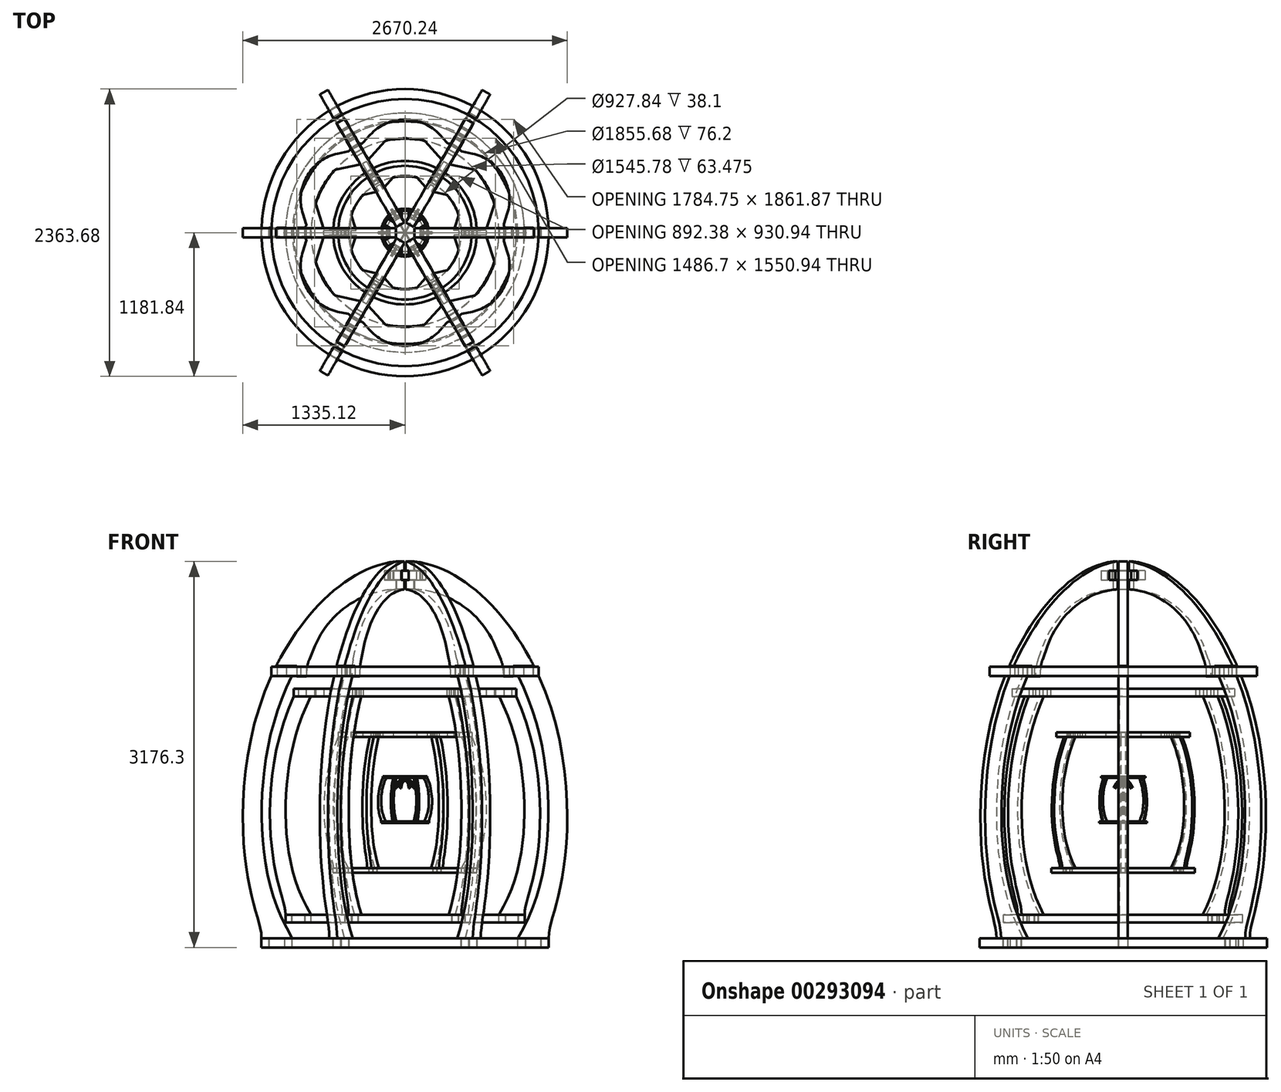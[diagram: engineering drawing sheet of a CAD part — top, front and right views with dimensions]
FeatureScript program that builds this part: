
annotation { "Feature Type Name" : "Feature", "Feature Type Description" : "" }
export const myFeature = defineFeature(function(context is Context, id is Id, definition is map)
    precondition{}
    {
        {
            var Q0;
            Q0=qCreatedBy(makeId("Front.planeOp"),FACE);
            var sketch = newSketch(context, id + "F0", { "sketchPlane" : qUnion([Q0])});
            skLineSegment(sketch, "E0", {"start": v(-1181.84, -1151.07) * mm, "end": v(-927.84, -1151.07) * mm});
            skFitSpline(sketch, "E1", {"points": [v(0, 1953.18) * mm, v(-1100.72, 1005.66) * mm, v(-1321.31, -446.19) * mm, v(-1216.83, -971.83) * mm, v(-1181.84, -1151.07) * mm], "startDerivative": vector(-4000.43, 5.06) * mm, "endDerivative": vector(0, -1489.55) * mm});
            skLineSegment(sketch, "E2", {"start": v(-1099.69, 1007.93) * mm, "end": v(-930.94, 1007.93) * mm});
            skLineSegment(sketch, "E3", {"start": v(-1181.84, -1151.07) * mm, "end": v(-1181.84, -1354.27) * mm});
            skLineSegment(sketch, "E4", {"start": v(-1181.84, -1354.27) * mm, "end": v(-877.04, -1354.27) * mm});
            skLineSegment(sketch, "E5", {"start": v(-877.04, -1354.27) * mm, "end": v(-877.04, -1252.67) * mm});
            skLineSegment(sketch, "E6", {"start": v(-877.04, -1252.67) * mm, "end": v(-927.84, -1252.67) * mm});
            skLineSegment(sketch, "E7", {"start": v(-927.84, -1252.67) * mm, "end": v(-927.84, -1151.07) * mm});
            skFitSpline(sketch, "E8.trimOffspring", {"points": [v(0, -1758.08) * mm, v(-927.84, -1151.07) * mm, v(-1179.31, -127.97) * mm, v(-917.89, 1033.92) * mm, v(0, 1800.5) * mm], "startDerivative": vector(-4973.2, 113.59) * mm, "endDerivative": vector(4756.7, 336.76) * mm});
            skLineSegment(sketch, "E9", {"start": v(-1023.33, 1160.33) * mm, "end": v(-848.12, 1160.33) * mm});
            skLineSegment(sketch, "E10", {"start": v(0, 1953.18) * mm, "end": v(0, 1800.5) * mm});
            skLineSegment(sketch, "E11.bottom", {"start": v(-1118.34, -1074.87) * mm, "end": v(-991.34, -1074.87) * mm});
            skLineSegment(sketch, "E11.top", {"start": v(-1118.34, -1227.27) * mm, "end": v(-991.34, -1227.27) * mm});
            skLineSegment(sketch, "E11.left", {"start": v(-1118.34, -1074.87) * mm, "end": v(-1118.34, -1227.27) * mm});
            skLineSegment(sketch, "E11.right", {"start": v(-991.34, -1074.87) * mm, "end": v(-991.34, -1227.27) * mm});
            skPoint(sketch, "E11.middle", {"position": v(-1054.84, -1151.07) * mm});
            skLineSegment(sketch, "E12.bottom", {"start": v(-1053.41, 1084.13) * mm, "end": v(-977.21, 1084.13) * mm});
            skLineSegment(sketch, "E12.top", {"start": v(-1053.41, 931.73) * mm, "end": v(-977.21, 931.73) * mm});
            skLineSegment(sketch, "E12.left", {"start": v(-1053.41, 1084.13) * mm, "end": v(-1053.41, 931.73) * mm});
            skLineSegment(sketch, "E12.right", {"start": v(-977.21, 1084.13) * mm, "end": v(-977.21, 931.73) * mm});
            skPoint(sketch, "E12.middle", {"position": v(-1015.31, 1007.93) * mm});
            skLineSegment(sketch, "E13", {"start": v(-891.46, 1084.13) * mm, "end": v(-1063.3, 1084.13) * mm});
            skLineSegment(sketch, "E14", {"start": v(-889.38, 1087.96) * mm, "end": v(-1061.37, 1087.96) * mm});
            skLineSegment(sketch, "E15", {"start": v(-76.2, 1949.03) * mm, "end": v(-76.2, 1791.14) * mm});
            skLineSegment(sketch, "E16", {"start": v(-76.2, 1791.14) * mm, "end": v(-76.2, 1796.63) * mm});
            skLineSegment(sketch, "E17", {"start": v(-76.2, 1796.63) * mm, "end": v(-127, 1796.63) * mm});
            skLineSegment(sketch, "E18", {"start": v(-127, 1796.63) * mm, "end": v(-127, 1872.83) * mm});
            skLineSegment(sketch, "E19", {"start": v(-127, 1872.83) * mm, "end": v(-76.2, 1872.83) * mm});
            skLineSegment(sketch, "E20", {"start": v(-889.38, 1087.96) * mm, "end": v(-810.8, 1087.96) * mm});
            skLineSegment(sketch, "E21", {"start": v(-810.8, 1087.96) * mm, "end": v(-680.59, 1399.26) * mm});
            skLineSegment(sketch, "E22", {"start": v(-810.8, 1087.96) * mm, "end": v(-810.8, 1004.5) * mm});
            skLineSegment(sketch, "E23", {"start": v(-889.38, 1087.96) * mm, "end": v(-889.38, 1004.5) * mm});
            skLineSegment(sketch, "E24", {"start": v(-889.38, 1004.5) * mm, "end": v(-810.8, 1004.5) * mm});
            skFitSpline(sketch, "E25", {"points": [v(-554.31, 1534.3) * mm, v(-76.2, 1720.43) * mm], "startDerivative": vector(464.08, 398.04) * mm, "endDerivative": vector(465.1, 29.66) * mm});
            skLineSegment(sketch, "E26", {"start": v(-76.2, 1720.43) * mm, "end": v(-76.2, 1791.14) * mm});
            skSolve(sketch);
        }
        {
            var Q0;
            {var subQ5=sQuery(id+"F0.wireOp",EDGE,"E12.bottom");Q0=makeQuery(id+"F0.imprint","IMPRINT",FACE,{"disambiguationData":[TD([[makeQuery(id+"F0.imprint","IMPRINT",EDGE,{"derivedFrom":subQ5}),-1.0]])]});}
            var Q1;
            {var subQ5=sQuery(id+"F0.wireOp",EDGE,"E11.top");Q1=makeQuery(id+"F0.imprint","IMPRINT",FACE,{"disambiguationData":[TD([[makeQuery(id+"F0.imprint","IMPRINT",EDGE,{"derivedFrom":subQ5}),1.0]])]});}
            var Q2;
            {var subQ0=sQuery(id+"F0.wireOp",EDGE,"E11.left");var subQ3=sQuery(id+"F0.wireOp",EDGE,"E0");var subQ4=makeQuery(id+"F0.imprint","INTERSECT",VERTEX,{"derivedFrom":[subQ3,subQ0]});Q2=makeQuery(id+"F0.imprint","IMPRINT",FACE,{"disambiguationData":[TD([[makeQuery(id+"F0.imprint","IMPRINT",EDGE,{"disambiguationData":[TD([[subQ4,-1.0]])],"derivedFrom":subQ3}),1.0]])]});}
            var Q3;
            {var subQ0=sQuery(id+"F0.wireOp",EDGE,"E2");var subQ1=sQuery(id+"F0.wireOp",EDGE,"E1");var subQ2=makeQuery(id+"F0.imprint","INTERSECT",VERTEX,{"derivedFrom":[subQ1,subQ0]});Q3=makeQuery(id+"F0.imprint","IMPRINT",FACE,{"disambiguationData":[TD([[makeQuery(id+"F0.imprint","IMPRINT",EDGE,{"disambiguationData":[TD([[subQ2,-1.0]])],"derivedFrom":subQ0}),-1.0]])]});}
            var Q4;
            {var subQ0=sQuery(id+"F0.wireOp",EDGE,"E8.trimOffspring");var subQ1=sQuery(id+"F0.wireOp",EDGE,"E2");var subQ2=makeQuery(id+"F0.imprint","INTERSECT",VERTEX,{"derivedFrom":[subQ1,subQ0]});Q4=makeQuery(id+"F0.imprint","IMPRINT",FACE,{"disambiguationData":[TD([[makeQuery(id+"F0.imprint","IMPRINT",EDGE,{"disambiguationData":[TD([[subQ2,1.0]])],"derivedFrom":subQ1}),-1.0]])]});}
            var Q5;
            {var subQ0=sQuery(id+"F0.wireOp",EDGE,"E12.left");var subQ5=sQuery(id+"F0.wireOp",EDGE,"E2");var subQ6=makeQuery(id+"F0.imprint","INTERSECT",VERTEX,{"derivedFrom":[subQ5,subQ0]});Q5=makeQuery(id+"F0.imprint","IMPRINT",FACE,{"disambiguationData":[TD([[makeQuery(id+"F0.imprint","IMPRINT",EDGE,{"disambiguationData":[TD([[subQ6,-1.0]])],"derivedFrom":subQ5}),-1.0]])]});}
            var Q6;
            {var subQ0=sQuery(id+"F0.wireOp",EDGE,"E12.left");var subQ1=sQuery(id+"F0.wireOp",EDGE,"E2");var subQ2=makeQuery(id+"F0.imprint","INTERSECT",VERTEX,{"derivedFrom":[subQ1,subQ0]});Q6=makeQuery(id+"F0.imprint","IMPRINT",FACE,{"disambiguationData":[TD([[makeQuery(id+"F0.imprint","IMPRINT",EDGE,{"disambiguationData":[TD([[subQ2,-1.0]])],"derivedFrom":subQ1}),1.0]])]});}
            extrude(context, id + "F1", {"entities" : qUnion([Q0, Q1, Q2, Q3, Q4, Q5, Q6]), "endBound" : BoundingType.SYMMETRIC, "depth" : 76.2 * mm});
        }
        {
            var Q0;
            Q0=makeQuery(id+"F1.opExtrude","SWEPT_BODY",BODY,{"disambiguationData":[OSD([sQuery(id+"F0.wireOp",EDGE,"E0"),sQuery(id+"F0.wireOp",EDGE,"E1"),sQuery(id+"F0.wireOp",EDGE,"E2"),sQuery(id+"F0.wireOp",EDGE,"E8.trimOffspring")])]});
            var Q1;
            Q1=sQuery(id+"F0.wireOp",EDGE,"E10");
            circularPattern(context, id + "F2", {"entities" : qUnion([Q0]), "axis" : qUnion([Q1]), "angle" : 360 * degree, "instanceCount" : 6, "equalSpace" : true});
        }
        {
            var Q0;
            Q0=qCreatedBy(makeId("Top.planeOp"),FACE);
            var Q1;
            Q1=sQuery(id+"F0.wireOp",VERTEX,"E8.trimOffspring.1.internal");
            cPlane(context, id + "F3", {"entities" : qUnion([Q0, Q1]), "cplaneType" : CPlaneType.PLANE_POINT, "offset" : 25.4 * mm, "width" : 152.4 * mm, "height" : 152.4 * mm});
        }
        {
            var Q0;
            Q0=qCreatedBy(id+"F3.planeOp",FACE);
            var sketch = newSketch(context, id + "F4", { "sketchPlane" : qUnion([Q0])});
            skCircle(sketch, "E27", {"center": v(0, 0) * mm, "radius": 1181.84 * mm});
            skCircle(sketch, "E28", {"center": v(0, 0) * mm, "radius": 927.84 * mm});
            skLineSegment(sketch, "E29.bottom", {"start": v(-1118.98, 38.73) * mm, "end": v(-990.7, 38.73) * mm});
            skLineSegment(sketch, "E29.top", {"start": v(-1118.98, -38.74) * mm, "end": v(-990.7, -38.74) * mm});
            skLineSegment(sketch, "E29.left", {"start": v(-1118.98, 38.73) * mm, "end": v(-1118.98, -38.74) * mm});
            skLineSegment(sketch, "E29.right", {"start": v(-990.7, 38.73) * mm, "end": v(-990.7, -38.74) * mm});
            skPoint(sketch, "E29.middle", {"position": v(-1054.84, 0) * mm});
            skLineSegment(sketch, "E30.1.0", {"start": v(-593.03, -949.7) * mm, "end": v(-528.9, -838.6) * mm});
            skLineSegment(sketch, "E30.1.1", {"start": v(-593.03, -949.7) * mm, "end": v(-525.94, -988.43) * mm});
            skLineSegment(sketch, "E30.1.2", {"start": v(-525.94, -988.43) * mm, "end": v(-461.8, -877.34) * mm});
            skLineSegment(sketch, "E30.1.3", {"start": v(-528.9, -838.6) * mm, "end": v(-461.8, -877.34) * mm});
            skLineSegment(sketch, "E30.2.0", {"start": v(525.94, -988.43) * mm, "end": v(461.8, -877.34) * mm});
            skLineSegment(sketch, "E30.2.1", {"start": v(525.94, -988.43) * mm, "end": v(593.03, -949.7) * mm});
            skLineSegment(sketch, "E30.2.2", {"start": v(593.03, -949.7) * mm, "end": v(528.9, -838.6) * mm});
            skLineSegment(sketch, "E30.2.3", {"start": v(461.8, -877.34) * mm, "end": v(528.9, -838.6) * mm});
            skLineSegment(sketch, "E30.3.0", {"start": v(1118.98, -38.74) * mm, "end": v(990.7, -38.74) * mm});
            skLineSegment(sketch, "E30.3.1", {"start": v(1118.98, -38.74) * mm, "end": v(1118.98, 38.73) * mm});
            skLineSegment(sketch, "E30.3.2", {"start": v(1118.98, 38.73) * mm, "end": v(990.7, 38.73) * mm});
            skLineSegment(sketch, "E30.3.3", {"start": v(990.7, -38.74) * mm, "end": v(990.7, 38.73) * mm});
            skLineSegment(sketch, "E30.4.0", {"start": v(593.03, 949.7) * mm, "end": v(528.9, 838.6) * mm});
            skLineSegment(sketch, "E30.4.1", {"start": v(593.03, 949.7) * mm, "end": v(525.94, 988.43) * mm});
            skLineSegment(sketch, "E30.4.2", {"start": v(525.94, 988.43) * mm, "end": v(461.8, 877.34) * mm});
            skLineSegment(sketch, "E30.4.3", {"start": v(528.9, 838.6) * mm, "end": v(461.8, 877.34) * mm});
            skLineSegment(sketch, "E30.5.0", {"start": v(-525.94, 988.43) * mm, "end": v(-461.8, 877.34) * mm});
            skLineSegment(sketch, "E30.5.1", {"start": v(-525.94, 988.43) * mm, "end": v(-593.03, 949.7) * mm});
            skLineSegment(sketch, "E30.5.2", {"start": v(-593.03, 949.7) * mm, "end": v(-528.9, 838.6) * mm});
            skLineSegment(sketch, "E30.5.3", {"start": v(-461.8, 877.34) * mm, "end": v(-528.9, 838.6) * mm});
            skSolve(sketch);
        }
        {
            var Q0;
            Q0=makeQuery(id+"F4.imprint","IMPRINT",FACE,{"disambiguationData":[TD([[makeQuery(id+"F4.imprint","IMPRINT",EDGE,{"derivedFrom":sQuery(id+"F4.wireOp",EDGE,"E27")}),1.0]])]});
            extrude(context, id + "F5", {"entities" : qUnion([Q0]), "oppositeDirection" : true, "depth" : 76.2 * mm});
        }
        {
            var Q0;
            Q0=qCreatedBy(makeId("Top.planeOp"),FACE);
            var Q1;
            Q1=sQuery(id+"F0.wireOp",VERTEX,"E2.end");
            cPlane(context, id + "F6", {"entities" : qUnion([Q0, Q1]), "cplaneType" : CPlaneType.PLANE_POINT, "offset" : 25.4 * mm, "width" : 152.4 * mm, "height" : 152.4 * mm});
        }
        {
            var Q0;
            Q0=qCreatedBy(id+"F6.planeOp",FACE);
            var sketch = newSketch(context, id + "F7", { "sketchPlane" : qUnion([Q0])});
            skCircle(sketch, "E31", {"center": v(0, 0) * mm, "radius": 1099.69 * mm});
            skCircle(sketch, "E32", {"center": v(0, 0) * mm, "radius": 930.94 * mm});
            skLineSegment(sketch, "E33.bottom", {"start": v(-1054.05, 38.74) * mm, "end": v(-976.58, 38.74) * mm});
            skLineSegment(sketch, "E33.top", {"start": v(-1054.05, -38.73) * mm, "end": v(-976.58, -38.73) * mm});
            skLineSegment(sketch, "E33.left", {"start": v(-1054.05, 38.74) * mm, "end": v(-1054.05, -38.73) * mm});
            skLineSegment(sketch, "E33.right", {"start": v(-976.58, 38.74) * mm, "end": v(-976.58, -38.73) * mm});
            skPoint(sketch, "E33.middle", {"position": v(-1015.31, 0) * mm});
            skLineSegment(sketch, "E34.1.0", {"start": v(-560.57, -893.46) * mm, "end": v(-521.83, -826.37) * mm});
            skLineSegment(sketch, "E34.1.1", {"start": v(-560.57, -893.46) * mm, "end": v(-493.48, -932.2) * mm});
            skLineSegment(sketch, "E34.1.2", {"start": v(-493.48, -932.2) * mm, "end": v(-454.74, -865.1) * mm});
            skLineSegment(sketch, "E34.1.3", {"start": v(-521.83, -826.37) * mm, "end": v(-454.74, -865.1) * mm});
            skLineSegment(sketch, "E34.2.0", {"start": v(493.48, -932.2) * mm, "end": v(454.74, -865.1) * mm});
            skLineSegment(sketch, "E34.2.1", {"start": v(493.48, -932.2) * mm, "end": v(560.57, -893.46) * mm});
            skLineSegment(sketch, "E34.2.2", {"start": v(560.57, -893.46) * mm, "end": v(521.83, -826.37) * mm});
            skLineSegment(sketch, "E34.2.3", {"start": v(454.74, -865.1) * mm, "end": v(521.83, -826.37) * mm});
            skLineSegment(sketch, "E34.3.0", {"start": v(1054.05, -38.74) * mm, "end": v(976.58, -38.74) * mm});
            skLineSegment(sketch, "E34.3.1", {"start": v(1054.05, -38.74) * mm, "end": v(1054.05, 38.73) * mm});
            skLineSegment(sketch, "E34.3.2", {"start": v(1054.05, 38.73) * mm, "end": v(976.58, 38.73) * mm});
            skLineSegment(sketch, "E34.3.3", {"start": v(976.58, -38.74) * mm, "end": v(976.58, 38.73) * mm});
            skLineSegment(sketch, "E34.4.0", {"start": v(560.57, 893.46) * mm, "end": v(521.83, 826.37) * mm});
            skLineSegment(sketch, "E34.4.1", {"start": v(560.57, 893.46) * mm, "end": v(493.48, 932.2) * mm});
            skLineSegment(sketch, "E34.4.2", {"start": v(493.48, 932.2) * mm, "end": v(454.74, 865.1) * mm});
            skLineSegment(sketch, "E34.4.3", {"start": v(521.83, 826.37) * mm, "end": v(454.74, 865.1) * mm});
            skLineSegment(sketch, "E34.5.0", {"start": v(-493.48, 932.2) * mm, "end": v(-454.74, 865.1) * mm});
            skLineSegment(sketch, "E34.5.1", {"start": v(-493.48, 932.2) * mm, "end": v(-560.57, 893.46) * mm});
            skLineSegment(sketch, "E34.5.2", {"start": v(-560.57, 893.46) * mm, "end": v(-521.83, 826.37) * mm});
            skLineSegment(sketch, "E34.5.3", {"start": v(-454.74, 865.1) * mm, "end": v(-521.83, 826.37) * mm});
            skLineSegment(sketch, "E35", {"start": v(-930.13, 38.73) * mm, "end": v(-803.13, 38.73) * mm});
            skLineSegment(sketch, "E36", {"start": v(-930.13, -38.74) * mm, "end": v(-803.13, -38.73) * mm});
            skLineSegment(sketch, "E37", {"start": v(-803.13, 38.74) * mm, "end": v(-803.13, -38.74) * mm, "construction": true});
            skLineSegment(sketch, "E38", {"start": v(-803.13, 0) * mm, "end": v(0, 0) * mm, "construction": true});
            skLineSegment(sketch, "E39", {"start": v(-803.13, 38.73) * mm, "end": v(-884.69, 289.77) * mm});
            skLineSegment(sketch, "E40", {"start": v(-803.13, -38.73) * mm, "end": v(-884.69, -289.77) * mm});
            skLineSegment(sketch, "E41.1.0", {"start": v(-435.11, -676.16) * mm, "end": v(-693.3, -621.28) * mm});
            skLineSegment(sketch, "E41.1.1", {"start": v(-498.61, -786.15) * mm, "end": v(-435.11, -676.16) * mm});
            skLineSegment(sketch, "E41.1.2", {"start": v(-431.52, -824.88) * mm, "end": v(-368.02, -714.9) * mm});
            skLineSegment(sketch, "E41.1.3", {"start": v(-368.02, -714.9) * mm, "end": v(-191.4, -911.05) * mm});
            skLineSegment(sketch, "E41.2.0", {"start": v(368.02, -714.9) * mm, "end": v(191.4, -911.05) * mm});
            skLineSegment(sketch, "E41.2.1", {"start": v(431.52, -824.88) * mm, "end": v(368.02, -714.9) * mm});
            skLineSegment(sketch, "E41.2.2", {"start": v(498.61, -786.15) * mm, "end": v(435.11, -676.16) * mm});
            skLineSegment(sketch, "E41.2.3", {"start": v(435.11, -676.16) * mm, "end": v(693.3, -621.28) * mm});
            skLineSegment(sketch, "E41.3.0", {"start": v(803.13, -38.74) * mm, "end": v(884.69, -289.77) * mm});
            skLineSegment(sketch, "E41.3.1", {"start": v(930.13, -38.74) * mm, "end": v(803.13, -38.74) * mm});
            skLineSegment(sketch, "E41.3.2", {"start": v(930.13, 38.73) * mm, "end": v(803.13, 38.73) * mm});
            skLineSegment(sketch, "E41.3.3", {"start": v(803.13, 38.73) * mm, "end": v(884.69, 289.77) * mm});
            skLineSegment(sketch, "E41.4.0", {"start": v(435.11, 676.16) * mm, "end": v(693.3, 621.28) * mm});
            skLineSegment(sketch, "E41.4.1", {"start": v(498.61, 786.15) * mm, "end": v(435.11, 676.16) * mm});
            skLineSegment(sketch, "E41.4.2", {"start": v(431.52, 824.88) * mm, "end": v(368.02, 714.9) * mm});
            skLineSegment(sketch, "E41.4.3", {"start": v(368.02, 714.9) * mm, "end": v(191.4, 911.05) * mm});
            skLineSegment(sketch, "E41.5.0", {"start": v(-368.02, 714.9) * mm, "end": v(-191.4, 911.05) * mm});
            skLineSegment(sketch, "E41.5.1", {"start": v(-431.52, 824.88) * mm, "end": v(-368.02, 714.9) * mm});
            skLineSegment(sketch, "E41.5.2", {"start": v(-498.61, 786.15) * mm, "end": v(-435.11, 676.16) * mm});
            skLineSegment(sketch, "E41.5.3", {"start": v(-435.11, 676.16) * mm, "end": v(-693.3, 621.28) * mm});
            skLineSegment(sketch, "E42", {"start": v(-892.38, 38.73) * mm, "end": v(-892.38, -38.74) * mm});
            skLineSegment(sketch, "E43.1.0", {"start": v(-479.73, -753.45) * mm, "end": v(-412.64, -792.19) * mm});
            skLineSegment(sketch, "E43.2.0", {"start": v(412.64, -792.19) * mm, "end": v(479.73, -753.45) * mm});
            skLineSegment(sketch, "E43.3.0", {"start": v(892.38, -38.74) * mm, "end": v(892.38, 38.73) * mm});
            skLineSegment(sketch, "E43.4.0", {"start": v(479.73, 753.45) * mm, "end": v(412.64, 792.19) * mm});
            skLineSegment(sketch, "E43.5.0", {"start": v(-412.64, 792.19) * mm, "end": v(-479.73, 753.45) * mm});
            skSolve(sketch);
        }
        {
            var Q0;
            Q0=makeQuery(id+"F7.imprint","IMPRINT",FACE,{"disambiguationData":[TD([[makeQuery(id+"F7.imprint","IMPRINT",EDGE,{"derivedFrom":sQuery(id+"F7.wireOp",EDGE,"E31")}),1.0]])]});
            var Q1;
            {var subQ0=sQuery(id+"F7.wireOp",EDGE,"E36");Q1=makeQuery(id+"F7.imprint","IMPRINT",FACE,{"disambiguationData":[TD([[makeQuery(id+"F7.imprint","IMPRINT",EDGE,{"derivedFrom":subQ0}),-1.0]])]});}
            var Q2;
            {var subQ0=sQuery(id+"F7.wireOp",EDGE,"E35");Q2=makeQuery(id+"F7.imprint","IMPRINT",FACE,{"disambiguationData":[TD([[makeQuery(id+"F7.imprint","IMPRINT",EDGE,{"derivedFrom":subQ0}),1.0]])]});}
            var Q3;
            {var subQ0=sQuery(id+"F7.wireOp",EDGE,"E41.5.2");Q3=makeQuery(id+"F7.imprint","IMPRINT",FACE,{"disambiguationData":[TD([[makeQuery(id+"F7.imprint","IMPRINT",EDGE,{"derivedFrom":subQ0}),-1.0]])]});}
            var Q4;
            {var subQ0=sQuery(id+"F7.wireOp",EDGE,"E41.5.0");Q4=makeQuery(id+"F7.imprint","IMPRINT",FACE,{"disambiguationData":[TD([[makeQuery(id+"F7.imprint","IMPRINT",EDGE,{"derivedFrom":subQ0}),1.0]])]});}
            var Q5;
            {var subQ0=sQuery(id+"F7.wireOp",EDGE,"E41.4.2");Q5=makeQuery(id+"F7.imprint","IMPRINT",FACE,{"disambiguationData":[TD([[makeQuery(id+"F7.imprint","IMPRINT",EDGE,{"derivedFrom":subQ0}),-1.0]])]});}
            var Q6;
            {var subQ0=sQuery(id+"F7.wireOp",EDGE,"E41.4.0");Q6=makeQuery(id+"F7.imprint","IMPRINT",FACE,{"disambiguationData":[TD([[makeQuery(id+"F7.imprint","IMPRINT",EDGE,{"derivedFrom":subQ0}),1.0]])]});}
            var Q7;
            {var subQ0=sQuery(id+"F7.wireOp",EDGE,"E41.3.2");Q7=makeQuery(id+"F7.imprint","IMPRINT",FACE,{"disambiguationData":[TD([[makeQuery(id+"F7.imprint","IMPRINT",EDGE,{"derivedFrom":subQ0}),-1.0]])]});}
            var Q8;
            {var subQ0=sQuery(id+"F7.wireOp",EDGE,"E41.3.0");Q8=makeQuery(id+"F7.imprint","IMPRINT",FACE,{"disambiguationData":[TD([[makeQuery(id+"F7.imprint","IMPRINT",EDGE,{"derivedFrom":subQ0}),1.0]])]});}
            var Q9;
            {var subQ0=sQuery(id+"F7.wireOp",EDGE,"E41.2.2");Q9=makeQuery(id+"F7.imprint","IMPRINT",FACE,{"disambiguationData":[TD([[makeQuery(id+"F7.imprint","IMPRINT",EDGE,{"derivedFrom":subQ0}),-1.0]])]});}
            var Q10;
            {var subQ0=sQuery(id+"F7.wireOp",EDGE,"E41.2.0");Q10=makeQuery(id+"F7.imprint","IMPRINT",FACE,{"disambiguationData":[TD([[makeQuery(id+"F7.imprint","IMPRINT",EDGE,{"derivedFrom":subQ0}),1.0]])]});}
            var Q11;
            {var subQ0=sQuery(id+"F7.wireOp",EDGE,"E41.1.2");Q11=makeQuery(id+"F7.imprint","IMPRINT",FACE,{"disambiguationData":[TD([[makeQuery(id+"F7.imprint","IMPRINT",EDGE,{"derivedFrom":subQ0}),-1.0]])]});}
            var Q12;
            {var subQ0=sQuery(id+"F7.wireOp",EDGE,"E41.1.0");Q12=makeQuery(id+"F7.imprint","IMPRINT",FACE,{"disambiguationData":[TD([[makeQuery(id+"F7.imprint","IMPRINT",EDGE,{"derivedFrom":subQ0}),1.0]])]});}
            var Q13;
            {var subQ3=sQuery(id+"F7.wireOp",EDGE,"E42");Q13=makeQuery(id+"F7.imprint","IMPRINT",FACE,{"disambiguationData":[TD([[makeQuery(id+"F7.imprint","IMPRINT",EDGE,{"derivedFrom":subQ3}),-1.0]])]});}
            var Q14;
            {var subQ5=sQuery(id+"F7.wireOp",EDGE,"E43.1.0");Q14=makeQuery(id+"F7.imprint","IMPRINT",FACE,{"disambiguationData":[TD([[makeQuery(id+"F7.imprint","IMPRINT",EDGE,{"derivedFrom":subQ5}),-1.0]])]});}
            var Q15;
            {var subQ5=sQuery(id+"F7.wireOp",EDGE,"E43.2.0");Q15=makeQuery(id+"F7.imprint","IMPRINT",FACE,{"disambiguationData":[TD([[makeQuery(id+"F7.imprint","IMPRINT",EDGE,{"derivedFrom":subQ5}),-1.0]])]});}
            var Q16;
            {var subQ5=sQuery(id+"F7.wireOp",EDGE,"E43.3.0");Q16=makeQuery(id+"F7.imprint","IMPRINT",FACE,{"disambiguationData":[TD([[makeQuery(id+"F7.imprint","IMPRINT",EDGE,{"derivedFrom":subQ5}),-1.0]])]});}
            var Q17;
            {var subQ5=sQuery(id+"F7.wireOp",EDGE,"E43.4.0");Q17=makeQuery(id+"F7.imprint","IMPRINT",FACE,{"disambiguationData":[TD([[makeQuery(id+"F7.imprint","IMPRINT",EDGE,{"derivedFrom":subQ5}),-1.0]])]});}
            var Q18;
            {var subQ5=sQuery(id+"F7.wireOp",EDGE,"E43.5.0");Q18=makeQuery(id+"F7.imprint","IMPRINT",FACE,{"disambiguationData":[TD([[makeQuery(id+"F7.imprint","IMPRINT",EDGE,{"derivedFrom":subQ5}),-1.0]])]});}
            extrude(context, id + "F8", {"entities" : qUnion([Q0, Q1, Q2, Q3, Q4, Q5, Q6, Q7, Q8, Q9, Q10, Q11, Q12, Q13, Q14, Q15, Q16, Q17, Q18]), "depth" : 76.2 * mm});
        }
        {
            var Q0;
            Q0=makeQuery(id+"F8.opExtrude","SWEPT_BODY",BODY,{"disambiguationData":[OSD([sQuery(id+"F7.wireOp",EDGE,"E31"),sQuery(id+"F7.wireOp",EDGE,"E32"),sQuery(id+"F7.wireOp",EDGE,"E33.bottom"),sQuery(id+"F7.wireOp",EDGE,"E33.top"),sQuery(id+"F7.wireOp",EDGE,"E33.left"),sQuery(id+"F7.wireOp",EDGE,"E33.right"),sQuery(id+"F7.wireOp",EDGE,"E34.1.0"),sQuery(id+"F7.wireOp",EDGE,"E34.1.1"),sQuery(id+"F7.wireOp",EDGE,"E34.1.2"),sQuery(id+"F7.wireOp",EDGE,"E34.1.3"),sQuery(id+"F7.wireOp",EDGE,"E34.2.0"),sQuery(id+"F7.wireOp",EDGE,"E34.2.1"),sQuery(id+"F7.wireOp",EDGE,"E34.2.2"),sQuery(id+"F7.wireOp",EDGE,"E34.2.3"),sQuery(id+"F7.wireOp",EDGE,"E34.3.0"),sQuery(id+"F7.wireOp",EDGE,"E34.3.1"),sQuery(id+"F7.wireOp",EDGE,"E34.3.2"),sQuery(id+"F7.wireOp",EDGE,"E34.3.3"),sQuery(id+"F7.wireOp",EDGE,"E34.4.0"),sQuery(id+"F7.wireOp",EDGE,"E34.4.1"),sQuery(id+"F7.wireOp",EDGE,"E34.4.2"),sQuery(id+"F7.wireOp",EDGE,"E34.4.3"),sQuery(id+"F7.wireOp",EDGE,"E34.5.0"),sQuery(id+"F7.wireOp",EDGE,"E34.5.1"),sQuery(id+"F7.wireOp",EDGE,"E34.5.2"),sQuery(id+"F7.wireOp",EDGE,"E34.5.3")])]});
            var Q1;
            Q1=makeQuery(id+"F1.opExtrude","SWEPT_BODY",BODY,{"disambiguationData":[OSD([sQuery(id+"F0.wireOp",EDGE,"E0"),sQuery(id+"F0.wireOp",EDGE,"E1"),sQuery(id+"F0.wireOp",EDGE,"E2"),sQuery(id+"F0.wireOp",EDGE,"E8.trimOffspring"),sQuery(id+"F0.wireOp",EDGE,"E11.top"),sQuery(id+"F0.wireOp",EDGE,"E11.left"),sQuery(id+"F0.wireOp",EDGE,"E11.right"),sQuery(id+"F0.wireOp",EDGE,"E12.bottom"),sQuery(id+"F0.wireOp",EDGE,"E12.left"),sQuery(id+"F0.wireOp",EDGE,"E12.right")])]});
            var Q2;
            Q2=makeQuery(id+"F2.opPattern","COPY",BODY,{"derivedFrom":makeQuery(id+"F1.opExtrude","SWEPT_BODY",BODY,{"disambiguationData":[OSD([sQuery(id+"F0.wireOp",EDGE,"E0"),sQuery(id+"F0.wireOp",EDGE,"E1"),sQuery(id+"F0.wireOp",EDGE,"E2"),sQuery(id+"F0.wireOp",EDGE,"E8.trimOffspring"),sQuery(id+"F0.wireOp",EDGE,"E11.top"),sQuery(id+"F0.wireOp",EDGE,"E11.left"),sQuery(id+"F0.wireOp",EDGE,"E11.right"),sQuery(id+"F0.wireOp",EDGE,"E12.bottom"),sQuery(id+"F0.wireOp",EDGE,"E12.left"),sQuery(id+"F0.wireOp",EDGE,"E12.right")])]}),"instanceName":"5"});
            var Q3;
            Q3=makeQuery(id+"F2.opPattern","COPY",BODY,{"derivedFrom":makeQuery(id+"F1.opExtrude","SWEPT_BODY",BODY,{"disambiguationData":[OSD([sQuery(id+"F0.wireOp",EDGE,"E0"),sQuery(id+"F0.wireOp",EDGE,"E1"),sQuery(id+"F0.wireOp",EDGE,"E2"),sQuery(id+"F0.wireOp",EDGE,"E8.trimOffspring"),sQuery(id+"F0.wireOp",EDGE,"E11.top"),sQuery(id+"F0.wireOp",EDGE,"E11.left"),sQuery(id+"F0.wireOp",EDGE,"E11.right"),sQuery(id+"F0.wireOp",EDGE,"E12.bottom"),sQuery(id+"F0.wireOp",EDGE,"E12.left"),sQuery(id+"F0.wireOp",EDGE,"E12.right")])]}),"instanceName":"1"});
            var Q4;
            Q4=makeQuery(id+"F2.opPattern","COPY",BODY,{"derivedFrom":makeQuery(id+"F1.opExtrude","SWEPT_BODY",BODY,{"disambiguationData":[OSD([sQuery(id+"F0.wireOp",EDGE,"E0"),sQuery(id+"F0.wireOp",EDGE,"E1"),sQuery(id+"F0.wireOp",EDGE,"E2"),sQuery(id+"F0.wireOp",EDGE,"E8.trimOffspring"),sQuery(id+"F0.wireOp",EDGE,"E11.top"),sQuery(id+"F0.wireOp",EDGE,"E11.left"),sQuery(id+"F0.wireOp",EDGE,"E11.right"),sQuery(id+"F0.wireOp",EDGE,"E12.bottom"),sQuery(id+"F0.wireOp",EDGE,"E12.left"),sQuery(id+"F0.wireOp",EDGE,"E12.right")])]}),"instanceName":"2"});
            var Q5;
            Q5=makeQuery(id+"F2.opPattern","COPY",BODY,{"derivedFrom":makeQuery(id+"F1.opExtrude","SWEPT_BODY",BODY,{"disambiguationData":[OSD([sQuery(id+"F0.wireOp",EDGE,"E0"),sQuery(id+"F0.wireOp",EDGE,"E1"),sQuery(id+"F0.wireOp",EDGE,"E2"),sQuery(id+"F0.wireOp",EDGE,"E8.trimOffspring"),sQuery(id+"F0.wireOp",EDGE,"E11.top"),sQuery(id+"F0.wireOp",EDGE,"E11.left"),sQuery(id+"F0.wireOp",EDGE,"E11.right"),sQuery(id+"F0.wireOp",EDGE,"E12.bottom"),sQuery(id+"F0.wireOp",EDGE,"E12.left"),sQuery(id+"F0.wireOp",EDGE,"E12.right")])]}),"instanceName":"3"});
            var Q6;
            Q6=makeQuery(id+"F2.opPattern","COPY",BODY,{"derivedFrom":makeQuery(id+"F1.opExtrude","SWEPT_BODY",BODY,{"disambiguationData":[OSD([sQuery(id+"F0.wireOp",EDGE,"E0"),sQuery(id+"F0.wireOp",EDGE,"E1"),sQuery(id+"F0.wireOp",EDGE,"E2"),sQuery(id+"F0.wireOp",EDGE,"E8.trimOffspring"),sQuery(id+"F0.wireOp",EDGE,"E11.top"),sQuery(id+"F0.wireOp",EDGE,"E11.left"),sQuery(id+"F0.wireOp",EDGE,"E11.right"),sQuery(id+"F0.wireOp",EDGE,"E12.bottom"),sQuery(id+"F0.wireOp",EDGE,"E12.left"),sQuery(id+"F0.wireOp",EDGE,"E12.right")])]}),"instanceName":"4"});
            var Q7;
            Q7=makeQuery(id+"F5.opExtrude","SWEPT_BODY",BODY,{"disambiguationData":[OSD([sQuery(id+"F4.wireOp",EDGE,"E27"),sQuery(id+"F4.wireOp",EDGE,"E28"),sQuery(id+"F4.wireOp",EDGE,"E29.bottom"),sQuery(id+"F4.wireOp",EDGE,"E29.top"),sQuery(id+"F4.wireOp",EDGE,"E29.left"),sQuery(id+"F4.wireOp",EDGE,"E29.right"),sQuery(id+"F4.wireOp",EDGE,"E30.1.0"),sQuery(id+"F4.wireOp",EDGE,"E30.1.1"),sQuery(id+"F4.wireOp",EDGE,"E30.1.2"),sQuery(id+"F4.wireOp",EDGE,"E30.1.3"),sQuery(id+"F4.wireOp",EDGE,"E30.2.0"),sQuery(id+"F4.wireOp",EDGE,"E30.2.1"),sQuery(id+"F4.wireOp",EDGE,"E30.2.2"),sQuery(id+"F4.wireOp",EDGE,"E30.2.3"),sQuery(id+"F4.wireOp",EDGE,"E30.3.0"),sQuery(id+"F4.wireOp",EDGE,"E30.3.1"),sQuery(id+"F4.wireOp",EDGE,"E30.3.2"),sQuery(id+"F4.wireOp",EDGE,"E30.3.3"),sQuery(id+"F4.wireOp",EDGE,"E30.4.0"),sQuery(id+"F4.wireOp",EDGE,"E30.4.1"),sQuery(id+"F4.wireOp",EDGE,"E30.4.2"),sQuery(id+"F4.wireOp",EDGE,"E30.4.3"),sQuery(id+"F4.wireOp",EDGE,"E30.5.0"),sQuery(id+"F4.wireOp",EDGE,"E30.5.1"),sQuery(id+"F4.wireOp",EDGE,"E30.5.2"),sQuery(id+"F4.wireOp",EDGE,"E30.5.3")])]});
            var Q8;
            Q8=qCreatedBy(makeId("Origin.pointOp"),VERTEX);
            transform(context, id + "F9", {"entities" : qUnion([Q0, Q1, Q2, Q3, Q4, Q5, Q6, Q7]), "transformType" : TransformType.SCALE_UNIFORMLY, "scale" : .1666, "scalePoint" : qUnion([Q8]), "makeCopy" : true});
        }
        {
            var Q0;
            Q0=makeQuery(id+"F8.opExtrude","SWEPT_BODY",BODY,{"disambiguationData":[OSD([sQuery(id+"F7.wireOp",EDGE,"E31"),sQuery(id+"F7.wireOp",EDGE,"E32"),sQuery(id+"F7.wireOp",EDGE,"E33.bottom"),sQuery(id+"F7.wireOp",EDGE,"E33.top"),sQuery(id+"F7.wireOp",EDGE,"E33.left"),sQuery(id+"F7.wireOp",EDGE,"E33.right"),sQuery(id+"F7.wireOp",EDGE,"E34.1.0"),sQuery(id+"F7.wireOp",EDGE,"E34.1.1"),sQuery(id+"F7.wireOp",EDGE,"E34.1.2"),sQuery(id+"F7.wireOp",EDGE,"E34.1.3"),sQuery(id+"F7.wireOp",EDGE,"E34.2.0"),sQuery(id+"F7.wireOp",EDGE,"E34.2.1"),sQuery(id+"F7.wireOp",EDGE,"E34.2.2"),sQuery(id+"F7.wireOp",EDGE,"E34.2.3"),sQuery(id+"F7.wireOp",EDGE,"E34.3.0"),sQuery(id+"F7.wireOp",EDGE,"E34.3.1"),sQuery(id+"F7.wireOp",EDGE,"E34.3.2"),sQuery(id+"F7.wireOp",EDGE,"E34.3.3"),sQuery(id+"F7.wireOp",EDGE,"E34.4.0"),sQuery(id+"F7.wireOp",EDGE,"E34.4.1"),sQuery(id+"F7.wireOp",EDGE,"E34.4.2"),sQuery(id+"F7.wireOp",EDGE,"E34.4.3"),sQuery(id+"F7.wireOp",EDGE,"E34.5.0"),sQuery(id+"F7.wireOp",EDGE,"E34.5.1"),sQuery(id+"F7.wireOp",EDGE,"E34.5.2"),sQuery(id+"F7.wireOp",EDGE,"E34.5.3")])]});
            var Q1;
            Q1=makeQuery(id+"F1.opExtrude","SWEPT_BODY",BODY,{"disambiguationData":[OSD([sQuery(id+"F0.wireOp",EDGE,"E0"),sQuery(id+"F0.wireOp",EDGE,"E1"),sQuery(id+"F0.wireOp",EDGE,"E2"),sQuery(id+"F0.wireOp",EDGE,"E8.trimOffspring"),sQuery(id+"F0.wireOp",EDGE,"E11.top"),sQuery(id+"F0.wireOp",EDGE,"E11.left"),sQuery(id+"F0.wireOp",EDGE,"E11.right"),sQuery(id+"F0.wireOp",EDGE,"E12.bottom"),sQuery(id+"F0.wireOp",EDGE,"E12.left"),sQuery(id+"F0.wireOp",EDGE,"E12.right")])]});
            var Q2;
            Q2=makeQuery(id+"F2.opPattern","COPY",BODY,{"derivedFrom":makeQuery(id+"F1.opExtrude","SWEPT_BODY",BODY,{"disambiguationData":[OSD([sQuery(id+"F0.wireOp",EDGE,"E0"),sQuery(id+"F0.wireOp",EDGE,"E1"),sQuery(id+"F0.wireOp",EDGE,"E2"),sQuery(id+"F0.wireOp",EDGE,"E8.trimOffspring"),sQuery(id+"F0.wireOp",EDGE,"E11.top"),sQuery(id+"F0.wireOp",EDGE,"E11.left"),sQuery(id+"F0.wireOp",EDGE,"E11.right"),sQuery(id+"F0.wireOp",EDGE,"E12.bottom"),sQuery(id+"F0.wireOp",EDGE,"E12.left"),sQuery(id+"F0.wireOp",EDGE,"E12.right")])]}),"instanceName":"1"});
            var Q3;
            Q3=makeQuery(id+"F2.opPattern","COPY",BODY,{"derivedFrom":makeQuery(id+"F1.opExtrude","SWEPT_BODY",BODY,{"disambiguationData":[OSD([sQuery(id+"F0.wireOp",EDGE,"E0"),sQuery(id+"F0.wireOp",EDGE,"E1"),sQuery(id+"F0.wireOp",EDGE,"E2"),sQuery(id+"F0.wireOp",EDGE,"E8.trimOffspring"),sQuery(id+"F0.wireOp",EDGE,"E11.top"),sQuery(id+"F0.wireOp",EDGE,"E11.left"),sQuery(id+"F0.wireOp",EDGE,"E11.right"),sQuery(id+"F0.wireOp",EDGE,"E12.bottom"),sQuery(id+"F0.wireOp",EDGE,"E12.left"),sQuery(id+"F0.wireOp",EDGE,"E12.right")])]}),"instanceName":"2"});
            var Q4;
            Q4=makeQuery(id+"F2.opPattern","COPY",BODY,{"derivedFrom":makeQuery(id+"F1.opExtrude","SWEPT_BODY",BODY,{"disambiguationData":[OSD([sQuery(id+"F0.wireOp",EDGE,"E0"),sQuery(id+"F0.wireOp",EDGE,"E1"),sQuery(id+"F0.wireOp",EDGE,"E2"),sQuery(id+"F0.wireOp",EDGE,"E8.trimOffspring"),sQuery(id+"F0.wireOp",EDGE,"E11.top"),sQuery(id+"F0.wireOp",EDGE,"E11.left"),sQuery(id+"F0.wireOp",EDGE,"E11.right"),sQuery(id+"F0.wireOp",EDGE,"E12.bottom"),sQuery(id+"F0.wireOp",EDGE,"E12.left"),sQuery(id+"F0.wireOp",EDGE,"E12.right")])]}),"instanceName":"3"});
            var Q5;
            Q5=makeQuery(id+"F2.opPattern","COPY",BODY,{"derivedFrom":makeQuery(id+"F1.opExtrude","SWEPT_BODY",BODY,{"disambiguationData":[OSD([sQuery(id+"F0.wireOp",EDGE,"E0"),sQuery(id+"F0.wireOp",EDGE,"E1"),sQuery(id+"F0.wireOp",EDGE,"E2"),sQuery(id+"F0.wireOp",EDGE,"E8.trimOffspring"),sQuery(id+"F0.wireOp",EDGE,"E11.top"),sQuery(id+"F0.wireOp",EDGE,"E11.left"),sQuery(id+"F0.wireOp",EDGE,"E11.right"),sQuery(id+"F0.wireOp",EDGE,"E12.bottom"),sQuery(id+"F0.wireOp",EDGE,"E12.left"),sQuery(id+"F0.wireOp",EDGE,"E12.right")])]}),"instanceName":"4"});
            var Q6;
            Q6=makeQuery(id+"F5.opExtrude","SWEPT_BODY",BODY,{"disambiguationData":[OSD([sQuery(id+"F4.wireOp",EDGE,"E27"),sQuery(id+"F4.wireOp",EDGE,"E28"),sQuery(id+"F4.wireOp",EDGE,"E29.bottom"),sQuery(id+"F4.wireOp",EDGE,"E29.top"),sQuery(id+"F4.wireOp",EDGE,"E29.left"),sQuery(id+"F4.wireOp",EDGE,"E29.right"),sQuery(id+"F4.wireOp",EDGE,"E30.1.0"),sQuery(id+"F4.wireOp",EDGE,"E30.1.1"),sQuery(id+"F4.wireOp",EDGE,"E30.1.2"),sQuery(id+"F4.wireOp",EDGE,"E30.1.3"),sQuery(id+"F4.wireOp",EDGE,"E30.2.0"),sQuery(id+"F4.wireOp",EDGE,"E30.2.1"),sQuery(id+"F4.wireOp",EDGE,"E30.2.2"),sQuery(id+"F4.wireOp",EDGE,"E30.2.3"),sQuery(id+"F4.wireOp",EDGE,"E30.3.0"),sQuery(id+"F4.wireOp",EDGE,"E30.3.1"),sQuery(id+"F4.wireOp",EDGE,"E30.3.2"),sQuery(id+"F4.wireOp",EDGE,"E30.3.3"),sQuery(id+"F4.wireOp",EDGE,"E30.4.0"),sQuery(id+"F4.wireOp",EDGE,"E30.4.1"),sQuery(id+"F4.wireOp",EDGE,"E30.4.2"),sQuery(id+"F4.wireOp",EDGE,"E30.4.3"),sQuery(id+"F4.wireOp",EDGE,"E30.5.0"),sQuery(id+"F4.wireOp",EDGE,"E30.5.1"),sQuery(id+"F4.wireOp",EDGE,"E30.5.2"),sQuery(id+"F4.wireOp",EDGE,"E30.5.3")])]});
            var Q7;
            Q7=makeQuery(id+"F2.opPattern","COPY",BODY,{"derivedFrom":makeQuery(id+"F1.opExtrude","SWEPT_BODY",BODY,{"disambiguationData":[OSD([sQuery(id+"F0.wireOp",EDGE,"E0"),sQuery(id+"F0.wireOp",EDGE,"E1"),sQuery(id+"F0.wireOp",EDGE,"E2"),sQuery(id+"F0.wireOp",EDGE,"E8.trimOffspring"),sQuery(id+"F0.wireOp",EDGE,"E11.top"),sQuery(id+"F0.wireOp",EDGE,"E11.left"),sQuery(id+"F0.wireOp",EDGE,"E11.right"),sQuery(id+"F0.wireOp",EDGE,"E12.bottom"),sQuery(id+"F0.wireOp",EDGE,"E12.left"),sQuery(id+"F0.wireOp",EDGE,"E12.right")])]}),"instanceName":"5"});
            var Q8;
            Q8=qCreatedBy(makeId("Origin.pointOp"),VERTEX);
            transform(context, id + "F10", {"entities" : qUnion([Q0, Q1, Q2, Q3, Q4, Q5, Q6, Q7]), "transformType" : TransformType.SCALE_UNIFORMLY, "scale" : .833, "scalePoint" : qUnion([Q8]), "makeCopy" : true});
        }
        {
            var Q0;
            Q0=makeQuery(id+"F8.opExtrude","SWEPT_BODY",BODY,{"disambiguationData":[OSD([sQuery(id+"F7.wireOp",EDGE,"E31"),sQuery(id+"F7.wireOp",EDGE,"E32"),sQuery(id+"F7.wireOp",EDGE,"E33.bottom"),sQuery(id+"F7.wireOp",EDGE,"E33.top"),sQuery(id+"F7.wireOp",EDGE,"E33.left"),sQuery(id+"F7.wireOp",EDGE,"E33.right"),sQuery(id+"F7.wireOp",EDGE,"E34.1.0"),sQuery(id+"F7.wireOp",EDGE,"E34.1.1"),sQuery(id+"F7.wireOp",EDGE,"E34.1.2"),sQuery(id+"F7.wireOp",EDGE,"E34.1.3"),sQuery(id+"F7.wireOp",EDGE,"E34.2.0"),sQuery(id+"F7.wireOp",EDGE,"E34.2.1"),sQuery(id+"F7.wireOp",EDGE,"E34.2.2"),sQuery(id+"F7.wireOp",EDGE,"E34.2.3"),sQuery(id+"F7.wireOp",EDGE,"E34.3.0"),sQuery(id+"F7.wireOp",EDGE,"E34.3.1"),sQuery(id+"F7.wireOp",EDGE,"E34.3.2"),sQuery(id+"F7.wireOp",EDGE,"E34.3.3"),sQuery(id+"F7.wireOp",EDGE,"E34.4.0"),sQuery(id+"F7.wireOp",EDGE,"E34.4.1"),sQuery(id+"F7.wireOp",EDGE,"E34.4.2"),sQuery(id+"F7.wireOp",EDGE,"E34.4.3"),sQuery(id+"F7.wireOp",EDGE,"E34.5.0"),sQuery(id+"F7.wireOp",EDGE,"E34.5.1"),sQuery(id+"F7.wireOp",EDGE,"E34.5.2"),sQuery(id+"F7.wireOp",EDGE,"E34.5.3")])]});
            var Q1;
            Q1=makeQuery(id+"F2.opPattern","COPY",BODY,{"derivedFrom":makeQuery(id+"F1.opExtrude","SWEPT_BODY",BODY,{"disambiguationData":[OSD([sQuery(id+"F0.wireOp",EDGE,"E0"),sQuery(id+"F0.wireOp",EDGE,"E1"),sQuery(id+"F0.wireOp",EDGE,"E2"),sQuery(id+"F0.wireOp",EDGE,"E8.trimOffspring"),sQuery(id+"F0.wireOp",EDGE,"E11.top"),sQuery(id+"F0.wireOp",EDGE,"E11.left"),sQuery(id+"F0.wireOp",EDGE,"E11.right"),sQuery(id+"F0.wireOp",EDGE,"E12.bottom"),sQuery(id+"F0.wireOp",EDGE,"E12.left"),sQuery(id+"F0.wireOp",EDGE,"E12.right")])]}),"instanceName":"5"});
            var Q2;
            Q2=makeQuery(id+"F1.opExtrude","SWEPT_BODY",BODY,{"disambiguationData":[OSD([sQuery(id+"F0.wireOp",EDGE,"E0"),sQuery(id+"F0.wireOp",EDGE,"E1"),sQuery(id+"F0.wireOp",EDGE,"E2"),sQuery(id+"F0.wireOp",EDGE,"E8.trimOffspring"),sQuery(id+"F0.wireOp",EDGE,"E11.top"),sQuery(id+"F0.wireOp",EDGE,"E11.left"),sQuery(id+"F0.wireOp",EDGE,"E11.right"),sQuery(id+"F0.wireOp",EDGE,"E12.bottom"),sQuery(id+"F0.wireOp",EDGE,"E12.left"),sQuery(id+"F0.wireOp",EDGE,"E12.right")])]});
            var Q3;
            Q3=makeQuery(id+"F2.opPattern","COPY",BODY,{"derivedFrom":makeQuery(id+"F1.opExtrude","SWEPT_BODY",BODY,{"disambiguationData":[OSD([sQuery(id+"F0.wireOp",EDGE,"E0"),sQuery(id+"F0.wireOp",EDGE,"E1"),sQuery(id+"F0.wireOp",EDGE,"E2"),sQuery(id+"F0.wireOp",EDGE,"E8.trimOffspring"),sQuery(id+"F0.wireOp",EDGE,"E11.top"),sQuery(id+"F0.wireOp",EDGE,"E11.left"),sQuery(id+"F0.wireOp",EDGE,"E11.right"),sQuery(id+"F0.wireOp",EDGE,"E12.bottom"),sQuery(id+"F0.wireOp",EDGE,"E12.left"),sQuery(id+"F0.wireOp",EDGE,"E12.right")])]}),"instanceName":"4"});
            var Q4;
            Q4=makeQuery(id+"F2.opPattern","COPY",BODY,{"derivedFrom":makeQuery(id+"F1.opExtrude","SWEPT_BODY",BODY,{"disambiguationData":[OSD([sQuery(id+"F0.wireOp",EDGE,"E0"),sQuery(id+"F0.wireOp",EDGE,"E1"),sQuery(id+"F0.wireOp",EDGE,"E2"),sQuery(id+"F0.wireOp",EDGE,"E8.trimOffspring"),sQuery(id+"F0.wireOp",EDGE,"E11.top"),sQuery(id+"F0.wireOp",EDGE,"E11.left"),sQuery(id+"F0.wireOp",EDGE,"E11.right"),sQuery(id+"F0.wireOp",EDGE,"E12.bottom"),sQuery(id+"F0.wireOp",EDGE,"E12.left"),sQuery(id+"F0.wireOp",EDGE,"E12.right")])]}),"instanceName":"3"});
            var Q5;
            Q5=makeQuery(id+"F2.opPattern","COPY",BODY,{"derivedFrom":makeQuery(id+"F1.opExtrude","SWEPT_BODY",BODY,{"disambiguationData":[OSD([sQuery(id+"F0.wireOp",EDGE,"E0"),sQuery(id+"F0.wireOp",EDGE,"E1"),sQuery(id+"F0.wireOp",EDGE,"E2"),sQuery(id+"F0.wireOp",EDGE,"E8.trimOffspring"),sQuery(id+"F0.wireOp",EDGE,"E11.top"),sQuery(id+"F0.wireOp",EDGE,"E11.left"),sQuery(id+"F0.wireOp",EDGE,"E11.right"),sQuery(id+"F0.wireOp",EDGE,"E12.bottom"),sQuery(id+"F0.wireOp",EDGE,"E12.left"),sQuery(id+"F0.wireOp",EDGE,"E12.right")])]}),"instanceName":"1"});
            var Q6;
            Q6=makeQuery(id+"F2.opPattern","COPY",BODY,{"derivedFrom":makeQuery(id+"F1.opExtrude","SWEPT_BODY",BODY,{"disambiguationData":[OSD([sQuery(id+"F0.wireOp",EDGE,"E0"),sQuery(id+"F0.wireOp",EDGE,"E1"),sQuery(id+"F0.wireOp",EDGE,"E2"),sQuery(id+"F0.wireOp",EDGE,"E8.trimOffspring"),sQuery(id+"F0.wireOp",EDGE,"E11.top"),sQuery(id+"F0.wireOp",EDGE,"E11.left"),sQuery(id+"F0.wireOp",EDGE,"E11.right"),sQuery(id+"F0.wireOp",EDGE,"E12.bottom"),sQuery(id+"F0.wireOp",EDGE,"E12.left"),sQuery(id+"F0.wireOp",EDGE,"E12.right")])]}),"instanceName":"2"});
            var Q7;
            Q7=makeQuery(id+"F5.opExtrude","SWEPT_BODY",BODY,{"disambiguationData":[OSD([sQuery(id+"F4.wireOp",EDGE,"E27"),sQuery(id+"F4.wireOp",EDGE,"E28"),sQuery(id+"F4.wireOp",EDGE,"E29.bottom"),sQuery(id+"F4.wireOp",EDGE,"E29.top"),sQuery(id+"F4.wireOp",EDGE,"E29.left"),sQuery(id+"F4.wireOp",EDGE,"E29.right"),sQuery(id+"F4.wireOp",EDGE,"E30.1.0"),sQuery(id+"F4.wireOp",EDGE,"E30.1.1"),sQuery(id+"F4.wireOp",EDGE,"E30.1.2"),sQuery(id+"F4.wireOp",EDGE,"E30.1.3"),sQuery(id+"F4.wireOp",EDGE,"E30.2.0"),sQuery(id+"F4.wireOp",EDGE,"E30.2.1"),sQuery(id+"F4.wireOp",EDGE,"E30.2.2"),sQuery(id+"F4.wireOp",EDGE,"E30.2.3"),sQuery(id+"F4.wireOp",EDGE,"E30.3.0"),sQuery(id+"F4.wireOp",EDGE,"E30.3.1"),sQuery(id+"F4.wireOp",EDGE,"E30.3.2"),sQuery(id+"F4.wireOp",EDGE,"E30.3.3"),sQuery(id+"F4.wireOp",EDGE,"E30.4.0"),sQuery(id+"F4.wireOp",EDGE,"E30.4.1"),sQuery(id+"F4.wireOp",EDGE,"E30.4.2"),sQuery(id+"F4.wireOp",EDGE,"E30.4.3"),sQuery(id+"F4.wireOp",EDGE,"E30.5.0"),sQuery(id+"F4.wireOp",EDGE,"E30.5.1"),sQuery(id+"F4.wireOp",EDGE,"E30.5.2"),sQuery(id+"F4.wireOp",EDGE,"E30.5.3")])]});
            var Q8;
            Q8=qCreatedBy(makeId("Origin.pointOp"),VERTEX);
            transform(context, id + "F11", {"entities" : qUnion([Q0, Q1, Q2, Q3, Q4, Q5, Q6, Q7]), "transformType" : TransformType.SCALE_UNIFORMLY, "scale" : .5, "scalePoint" : qUnion([Q8]), "makeCopy" : true});
        }
        {
            var Q0;
            {var subQ4=sQuery(id+"F0.wireOp",EDGE,"E9");Q0=makeQuery(id+"F0.imprint","IMPRINT",FACE,{"disambiguationData":[TD([[makeQuery(id+"F0.imprint","IMPRINT",EDGE,{"derivedFrom":subQ4}),-1.0]])]});}
            var Q1;
            {var subQ2=sQuery(id+"F0.wireOp",EDGE,"E9");Q1=makeQuery(id+"F0.imprint","IMPRINT",FACE,{"disambiguationData":[TD([[makeQuery(id+"F0.imprint","IMPRINT",EDGE,{"derivedFrom":subQ2}),1.0]])]});}
            var Q2;
            {var subQ2=sQuery(id+"F0.wireOp",EDGE,"E20");Q2=makeQuery(id+"F0.imprint","IMPRINT",FACE,{"disambiguationData":[TD([[makeQuery(id+"F0.imprint","IMPRINT",EDGE,{"derivedFrom":subQ2}),1.0]])]});}
            var Q3;
            Q3=makeQuery(id+"F0.imprint","IMPRINT",FACE,{"disambiguationData":[TD([[makeQuery(id+"F0.imprint","IMPRINT",EDGE,{"derivedFrom":sQuery(id+"F0.wireOp",EDGE,"E20")}),-1.0]])]});
            var Q4;
            {var subQ2=sQuery(id+"F0.wireOp",EDGE,"E25");Q4=makeQuery(id+"F0.imprint","IMPRINT",FACE,{"disambiguationData":[TD([[makeQuery(id+"F0.imprint","IMPRINT",EDGE,{"derivedFrom":subQ2}),1.0]])]});}
            extrude(context, id + "F12", {"entities" : qUnion([Q0, Q1, Q2, Q3, Q4]), "operationType" : NewBodyOperationType.ADD, "endBound" : BoundingType.SYMMETRIC, "depth" : 76.2 * mm});
        }
        {
            var Q0;
            Q0=makeQuery(id+"F12.opExtrude","SWEPT_EDGE",EDGE,{"disambiguationData":[OSD([sQuery(id+"F0.wireOp",EDGE,"E8.trimOffspring"),sQuery(id+"F0.wireOp",EDGE,"E21")])]});
            fillet(context, id + "F13", {"entities" : qUnion([Q0]), "radius" : 762 * mm, "tangentPropagation" : true, "allowEdgeOverflow" : false});
        }
        {
            var Q0;
            Q0=makeQuery(id+"F12.opExtrude","SWEPT_EDGE",EDGE,{"disambiguationData":[OSD([sQuery(id+"F0.wireOp",EDGE,"E20"),sQuery(id+"F0.wireOp",EDGE,"E21"),sQuery(id+"F0.wireOp",EDGE,"E22")])]});
            fillet(context, id + "F14", {"entities" : qUnion([Q0]), "radius" : 304.8 * mm, "tangentPropagation" : true, "allowEdgeOverflow" : false});
        }
        {
            var Q0;
            Q0=makeQuery(id+"F12.opExtrude","SWEPT_BODY",BODY,{"disambiguationData":[OSD([sQuery(id+"F0.wireOp",EDGE,"E1"),sQuery(id+"F0.wireOp",EDGE,"E8.trimOffspring"),sQuery(id+"F0.wireOp",EDGE,"E10"),sQuery(id+"F0.wireOp",EDGE,"E14")])]});
            var Q1;
            Q1=sQuery(id+"F0.wireOp",EDGE,"E10");
            circularPattern(context, id + "F15", {"entities" : qUnion([Q0]), "axis" : qUnion([Q1]), "angle" : 360 * degree, "instanceCount" : 6, "equalSpace" : true});
        }
        {
            var Q0;
            Q0=makeQuery(id+"F8.opExtrude","SWEPT_EDGE",EDGE,{"disambiguationData":[OSD([sQuery(id+"F7.wireOp",EDGE,"E32"),sQuery(id+"F7.wireOp",EDGE,"E40")])]});
            var Q1;
            Q1=makeQuery(id+"F8.opExtrude","SWEPT_EDGE",EDGE,{"disambiguationData":[OSD([sQuery(id+"F7.wireOp",EDGE,"E32"),sQuery(id+"F7.wireOp",EDGE,"E39")])]});
            var Q2;
            Q2=makeQuery(id+"F8.opExtrude","SWEPT_EDGE",EDGE,{"disambiguationData":[OSD([sQuery(id+"F7.wireOp",EDGE,"E32"),sQuery(id+"F7.wireOp",EDGE,"E41.5.3")])]});
            var Q3;
            Q3=makeQuery(id+"F8.opExtrude","SWEPT_EDGE",EDGE,{"disambiguationData":[OSD([sQuery(id+"F7.wireOp",EDGE,"E32"),sQuery(id+"F7.wireOp",EDGE,"E41.5.0")])]});
            var Q4;
            Q4=makeQuery(id+"F8.opExtrude","SWEPT_EDGE",EDGE,{"disambiguationData":[OSD([sQuery(id+"F7.wireOp",EDGE,"E32"),sQuery(id+"F7.wireOp",EDGE,"E41.4.3")])]});
            var Q5;
            Q5=makeQuery(id+"F8.opExtrude","SWEPT_EDGE",EDGE,{"disambiguationData":[OSD([sQuery(id+"F7.wireOp",EDGE,"E32"),sQuery(id+"F7.wireOp",EDGE,"E41.4.0")])]});
            var Q6;
            Q6=makeQuery(id+"F8.opExtrude","SWEPT_EDGE",EDGE,{"disambiguationData":[OSD([sQuery(id+"F7.wireOp",EDGE,"E32"),sQuery(id+"F7.wireOp",EDGE,"E41.3.3")])]});
            var Q7;
            Q7=makeQuery(id+"F8.opExtrude","SWEPT_EDGE",EDGE,{"disambiguationData":[OSD([sQuery(id+"F7.wireOp",EDGE,"E32"),sQuery(id+"F7.wireOp",EDGE,"E41.3.0")])]});
            var Q8;
            Q8=makeQuery(id+"F8.opExtrude","SWEPT_EDGE",EDGE,{"disambiguationData":[OSD([sQuery(id+"F7.wireOp",EDGE,"E32"),sQuery(id+"F7.wireOp",EDGE,"E41.2.3")])]});
            var Q9;
            Q9=makeQuery(id+"F8.opExtrude","SWEPT_EDGE",EDGE,{"disambiguationData":[OSD([sQuery(id+"F7.wireOp",EDGE,"E32"),sQuery(id+"F7.wireOp",EDGE,"E41.2.0")])]});
            var Q10;
            Q10=makeQuery(id+"F8.opExtrude","SWEPT_EDGE",EDGE,{"disambiguationData":[OSD([sQuery(id+"F7.wireOp",EDGE,"E32"),sQuery(id+"F7.wireOp",EDGE,"E41.1.3")])]});
            var Q11;
            Q11=makeQuery(id+"F8.opExtrude","SWEPT_EDGE",EDGE,{"disambiguationData":[OSD([sQuery(id+"F7.wireOp",EDGE,"E32"),sQuery(id+"F7.wireOp",EDGE,"E41.1.0")])]});
            fillet(context, id + "F16", {"entities" : qUnion([Q0, Q1, Q2, Q3, Q4, Q5, Q6, Q7, Q8, Q9, Q10, Q11]), "radius" : 381 * mm, "tangentPropagation" : true, "allowEdgeOverflow" : false});
        }
        {
            var Q0;
            Q0=makeQuery(id+"F8.opExtrude","SWEPT_EDGE",EDGE,{"disambiguationData":[OSD([sQuery(id+"F7.wireOp",EDGE,"E41.4.0"),sQuery(id+"F7.wireOp",EDGE,"E41.4.1")])]});
            var Q1;
            Q1=makeQuery(id+"F8.opExtrude","SWEPT_EDGE",EDGE,{"disambiguationData":[OSD([sQuery(id+"F7.wireOp",EDGE,"E41.4.2"),sQuery(id+"F7.wireOp",EDGE,"E41.4.3")])]});
            var Q2;
            Q2=makeQuery(id+"F8.opExtrude","SWEPT_EDGE",EDGE,{"disambiguationData":[OSD([sQuery(id+"F7.wireOp",EDGE,"E41.5.0"),sQuery(id+"F7.wireOp",EDGE,"E41.5.1")])]});
            var Q3;
            Q3=makeQuery(id+"F8.opExtrude","SWEPT_EDGE",EDGE,{"disambiguationData":[OSD([sQuery(id+"F7.wireOp",EDGE,"E41.5.2"),sQuery(id+"F7.wireOp",EDGE,"E41.5.3")])]});
            var Q4;
            Q4=makeQuery(id+"F8.opExtrude","SWEPT_EDGE",EDGE,{"disambiguationData":[OSD([sQuery(id+"F7.wireOp",EDGE,"E35"),sQuery(id+"F7.wireOp",EDGE,"E39")])]});
            var Q5;
            Q5=makeQuery(id+"F8.opExtrude","SWEPT_EDGE",EDGE,{"disambiguationData":[OSD([sQuery(id+"F7.wireOp",EDGE,"E36"),sQuery(id+"F7.wireOp",EDGE,"E40")])]});
            var Q6;
            Q6=makeQuery(id+"F8.opExtrude","SWEPT_EDGE",EDGE,{"disambiguationData":[OSD([sQuery(id+"F7.wireOp",EDGE,"E41.1.0"),sQuery(id+"F7.wireOp",EDGE,"E41.1.1")])]});
            var Q7;
            Q7=makeQuery(id+"F8.opExtrude","SWEPT_EDGE",EDGE,{"disambiguationData":[OSD([sQuery(id+"F7.wireOp",EDGE,"E41.1.2"),sQuery(id+"F7.wireOp",EDGE,"E41.1.3")])]});
            var Q8;
            Q8=makeQuery(id+"F8.opExtrude","SWEPT_EDGE",EDGE,{"disambiguationData":[OSD([sQuery(id+"F7.wireOp",EDGE,"E41.2.0"),sQuery(id+"F7.wireOp",EDGE,"E41.2.1")])]});
            var Q9;
            Q9=makeQuery(id+"F8.opExtrude","SWEPT_EDGE",EDGE,{"disambiguationData":[OSD([sQuery(id+"F7.wireOp",EDGE,"E41.2.2"),sQuery(id+"F7.wireOp",EDGE,"E41.2.3")])]});
            var Q10;
            Q10=makeQuery(id+"F8.opExtrude","SWEPT_EDGE",EDGE,{"disambiguationData":[OSD([sQuery(id+"F7.wireOp",EDGE,"E41.3.0"),sQuery(id+"F7.wireOp",EDGE,"E41.3.1")])]});
            var Q11;
            Q11=makeQuery(id+"F8.opExtrude","SWEPT_EDGE",EDGE,{"disambiguationData":[OSD([sQuery(id+"F7.wireOp",EDGE,"E41.3.2"),sQuery(id+"F7.wireOp",EDGE,"E41.3.3")])]});
            fillet(context, id + "F17", {"entities" : qUnion([Q0, Q1, Q2, Q3, Q4, Q5, Q6, Q7, Q8, Q9, Q10, Q11]), "radius" : 25.4 * mm, "tangentPropagation" : true, "allowEdgeOverflow" : false});
        }
        {
            var Q0;
            Q0=makeQuery(id+"F15.opPattern","COPY",FACE,{"derivedFrom":makeQuery(id+"F12.opExtrude","SWEPT_FACE",FACE,{"disambiguationData":[OSD([sQuery(id+"F0.wireOp",EDGE,"E17")])]}),"instanceName":"5"});
            var sketch = newSketch(context, id + "F18", { "sketchPlane" : qUnion([Q0])});
            skCircle(sketch, "E44", {"center": v(0, 0) * mm, "radius": 127 * mm});
            skLineSegment(sketch, "E45", {"start": v(-121.45, 37.13) * mm, "end": v(-170.95, 65.7) * mm});
            skLineSegment(sketch, "E46", {"start": v(-170.95, 65.7) * mm, "end": v(-142.37, 115.2) * mm});
            skLineSegment(sketch, "E47", {"start": v(-142.37, 115.2) * mm, "end": v(-92.88, 86.62) * mm});
            skLineSegment(sketch, "E48", {"start": v(-156.66, 90.45) * mm, "end": v(0, 0) * mm});
            skLineSegment(sketch, "E49", {"start": v(0, 0) * mm, "end": v(-54.91, 0) * mm, "construction": true});
            skLineSegment(sketch, "E50.1.0", {"start": v(-170.95, -65.7) * mm, "end": v(-121.45, -37.13) * mm});
            skLineSegment(sketch, "E50.1.1", {"start": v(-142.37, -115.2) * mm, "end": v(-170.95, -65.7) * mm});
            skLineSegment(sketch, "E50.1.2", {"start": v(-92.88, -86.62) * mm, "end": v(-142.37, -115.2) * mm});
            skLineSegment(sketch, "E50.2.0", {"start": v(-28.57, -180.9) * mm, "end": v(-28.57, -123.74) * mm});
            skLineSegment(sketch, "E50.2.1", {"start": v(28.58, -180.9) * mm, "end": v(-28.57, -180.9) * mm});
            skLineSegment(sketch, "E50.2.2", {"start": v(28.58, -123.74) * mm, "end": v(28.58, -180.9) * mm});
            skLineSegment(sketch, "E50.3.0", {"start": v(142.37, -115.2) * mm, "end": v(92.88, -86.62) * mm});
            skLineSegment(sketch, "E50.3.1", {"start": v(170.95, -65.7) * mm, "end": v(142.37, -115.2) * mm});
            skLineSegment(sketch, "E50.3.2", {"start": v(121.45, -37.13) * mm, "end": v(170.95, -65.7) * mm});
            skLineSegment(sketch, "E50.4.0", {"start": v(170.95, 65.7) * mm, "end": v(121.45, 37.13) * mm});
            skLineSegment(sketch, "E50.4.1", {"start": v(142.37, 115.2) * mm, "end": v(170.95, 65.7) * mm});
            skLineSegment(sketch, "E50.4.2", {"start": v(92.88, 86.62) * mm, "end": v(142.37, 115.2) * mm});
            skLineSegment(sketch, "E50.5.0", {"start": v(28.57, 180.9) * mm, "end": v(28.57, 123.74) * mm});
            skLineSegment(sketch, "E50.5.1", {"start": v(-28.58, 180.9) * mm, "end": v(28.57, 180.9) * mm});
            skLineSegment(sketch, "E50.5.2", {"start": v(-28.58, 123.74) * mm, "end": v(-28.58, 180.9) * mm});
            skSolve(sketch);
        }
        {
            var Q0;
            Q0=qSketchRegion(id+"F18",true);
            extrude(context, id + "F19", {"entities" : qUnion([Q0]), "depth" : 76.2 * mm});
        }
        {
            var Q0;
            Q0=makeQuery(id+"F15.opPattern","COPY",BODY,{"derivedFrom":makeQuery(id+"F12.opExtrude","SWEPT_BODY",BODY,{"disambiguationData":[OSD([sQuery(id+"F0.wireOp",EDGE,"E1"),sQuery(id+"F0.wireOp",EDGE,"E8.trimOffspring"),sQuery(id+"F0.wireOp",EDGE,"E14"),sQuery(id+"F0.wireOp",EDGE,"E15"),sQuery(id+"F0.wireOp",EDGE,"E16"),sQuery(id+"F0.wireOp",EDGE,"E17"),sQuery(id+"F0.wireOp",EDGE,"E18"),sQuery(id+"F0.wireOp",EDGE,"E19"),sQuery(id+"F0.wireOp",EDGE,"E21"),sQuery(id+"F0.wireOp",EDGE,"E22"),sQuery(id+"F0.wireOp",EDGE,"E23"),sQuery(id+"F0.wireOp",EDGE,"E24"),sQuery(id+"F0.wireOp",EDGE,"E25"),sQuery(id+"F0.wireOp",EDGE,"E26")])]}),"instanceName":"5"});
            var Q1;
            Q1=makeQuery(id+"F12.opExtrude","SWEPT_BODY",BODY,{"disambiguationData":[OSD([sQuery(id+"F0.wireOp",EDGE,"E1"),sQuery(id+"F0.wireOp",EDGE,"E8.trimOffspring"),sQuery(id+"F0.wireOp",EDGE,"E14"),sQuery(id+"F0.wireOp",EDGE,"E15"),sQuery(id+"F0.wireOp",EDGE,"E16"),sQuery(id+"F0.wireOp",EDGE,"E17"),sQuery(id+"F0.wireOp",EDGE,"E18"),sQuery(id+"F0.wireOp",EDGE,"E19"),sQuery(id+"F0.wireOp",EDGE,"E21"),sQuery(id+"F0.wireOp",EDGE,"E22"),sQuery(id+"F0.wireOp",EDGE,"E23"),sQuery(id+"F0.wireOp",EDGE,"E24"),sQuery(id+"F0.wireOp",EDGE,"E25"),sQuery(id+"F0.wireOp",EDGE,"E26")])]});
            var Q2;
            Q2=makeQuery(id+"F15.opPattern","COPY",BODY,{"derivedFrom":makeQuery(id+"F12.opExtrude","SWEPT_BODY",BODY,{"disambiguationData":[OSD([sQuery(id+"F0.wireOp",EDGE,"E1"),sQuery(id+"F0.wireOp",EDGE,"E8.trimOffspring"),sQuery(id+"F0.wireOp",EDGE,"E14"),sQuery(id+"F0.wireOp",EDGE,"E15"),sQuery(id+"F0.wireOp",EDGE,"E16"),sQuery(id+"F0.wireOp",EDGE,"E17"),sQuery(id+"F0.wireOp",EDGE,"E18"),sQuery(id+"F0.wireOp",EDGE,"E19"),sQuery(id+"F0.wireOp",EDGE,"E21"),sQuery(id+"F0.wireOp",EDGE,"E22"),sQuery(id+"F0.wireOp",EDGE,"E23"),sQuery(id+"F0.wireOp",EDGE,"E24"),sQuery(id+"F0.wireOp",EDGE,"E25"),sQuery(id+"F0.wireOp",EDGE,"E26")])]}),"instanceName":"3"});
            var Q3;
            Q3=makeQuery(id+"F15.opPattern","COPY",BODY,{"derivedFrom":makeQuery(id+"F12.opExtrude","SWEPT_BODY",BODY,{"disambiguationData":[OSD([sQuery(id+"F0.wireOp",EDGE,"E1"),sQuery(id+"F0.wireOp",EDGE,"E8.trimOffspring"),sQuery(id+"F0.wireOp",EDGE,"E14"),sQuery(id+"F0.wireOp",EDGE,"E15"),sQuery(id+"F0.wireOp",EDGE,"E16"),sQuery(id+"F0.wireOp",EDGE,"E17"),sQuery(id+"F0.wireOp",EDGE,"E18"),sQuery(id+"F0.wireOp",EDGE,"E19"),sQuery(id+"F0.wireOp",EDGE,"E21"),sQuery(id+"F0.wireOp",EDGE,"E22"),sQuery(id+"F0.wireOp",EDGE,"E23"),sQuery(id+"F0.wireOp",EDGE,"E24"),sQuery(id+"F0.wireOp",EDGE,"E25"),sQuery(id+"F0.wireOp",EDGE,"E26")])]}),"instanceName":"1"});
            var Q4;
            Q4=makeQuery(id+"F15.opPattern","COPY",BODY,{"derivedFrom":makeQuery(id+"F12.opExtrude","SWEPT_BODY",BODY,{"disambiguationData":[OSD([sQuery(id+"F0.wireOp",EDGE,"E1"),sQuery(id+"F0.wireOp",EDGE,"E8.trimOffspring"),sQuery(id+"F0.wireOp",EDGE,"E14"),sQuery(id+"F0.wireOp",EDGE,"E15"),sQuery(id+"F0.wireOp",EDGE,"E16"),sQuery(id+"F0.wireOp",EDGE,"E17"),sQuery(id+"F0.wireOp",EDGE,"E18"),sQuery(id+"F0.wireOp",EDGE,"E19"),sQuery(id+"F0.wireOp",EDGE,"E21"),sQuery(id+"F0.wireOp",EDGE,"E22"),sQuery(id+"F0.wireOp",EDGE,"E23"),sQuery(id+"F0.wireOp",EDGE,"E24"),sQuery(id+"F0.wireOp",EDGE,"E25"),sQuery(id+"F0.wireOp",EDGE,"E26")])]}),"instanceName":"2"});
            var Q5;
            Q5=makeQuery(id+"F15.opPattern","COPY",BODY,{"derivedFrom":makeQuery(id+"F12.opExtrude","SWEPT_BODY",BODY,{"disambiguationData":[OSD([sQuery(id+"F0.wireOp",EDGE,"E1"),sQuery(id+"F0.wireOp",EDGE,"E8.trimOffspring"),sQuery(id+"F0.wireOp",EDGE,"E14"),sQuery(id+"F0.wireOp",EDGE,"E15"),sQuery(id+"F0.wireOp",EDGE,"E16"),sQuery(id+"F0.wireOp",EDGE,"E17"),sQuery(id+"F0.wireOp",EDGE,"E18"),sQuery(id+"F0.wireOp",EDGE,"E19"),sQuery(id+"F0.wireOp",EDGE,"E21"),sQuery(id+"F0.wireOp",EDGE,"E22"),sQuery(id+"F0.wireOp",EDGE,"E23"),sQuery(id+"F0.wireOp",EDGE,"E24"),sQuery(id+"F0.wireOp",EDGE,"E25"),sQuery(id+"F0.wireOp",EDGE,"E26")])]}),"instanceName":"4"});
            var Q6;
            Q6=makeQuery(id+"F19.opExtrude","SWEPT_BODY",BODY,{"disambiguationData":[OSD([sQuery(id+"F18.wireOp",EDGE,"E44"),sQuery(id+"F18.wireOp",EDGE,"E45"),sQuery(id+"F18.wireOp",EDGE,"E46"),sQuery(id+"F18.wireOp",EDGE,"E47"),sQuery(id+"F18.wireOp",EDGE,"E50.1.0"),sQuery(id+"F18.wireOp",EDGE,"E50.1.1"),sQuery(id+"F18.wireOp",EDGE,"E50.1.2"),sQuery(id+"F18.wireOp",EDGE,"E50.2.0"),sQuery(id+"F18.wireOp",EDGE,"E50.2.1"),sQuery(id+"F18.wireOp",EDGE,"E50.2.2"),sQuery(id+"F18.wireOp",EDGE,"E50.3.0"),sQuery(id+"F18.wireOp",EDGE,"E50.3.1"),sQuery(id+"F18.wireOp",EDGE,"E50.3.2"),sQuery(id+"F18.wireOp",EDGE,"E50.4.0"),sQuery(id+"F18.wireOp",EDGE,"E50.4.1"),sQuery(id+"F18.wireOp",EDGE,"E50.4.2"),sQuery(id+"F18.wireOp",EDGE,"E50.5.0"),sQuery(id+"F18.wireOp",EDGE,"E50.5.1"),sQuery(id+"F18.wireOp",EDGE,"E50.5.2")])]});
            var Q7;
            Q7=qCreatedBy(makeId("Origin.pointOp"),VERTEX);
            transform(context, id + "F20", {"entities" : qUnion([Q0, Q1, Q2, Q3, Q4, Q5, Q6]), "transformType" : TransformType.SCALE_UNIFORMLY, "scale" : 1 / 12, "scalePoint" : qUnion([Q7]), "makeCopy" : true});
        }
        {
            var Q0;
            Q0=makeQuery(id+"F10.opPattern","COPY",EDGE,{"derivedFrom":makeQuery(id+"F8.opExtrude","SWEPT_EDGE",EDGE,{"disambiguationData":[OSD([sQuery(id+"F7.wireOp",EDGE,"E32"),sQuery(id+"F7.wireOp",EDGE,"E41.3.3")])]}),"instanceName":"1"});
            var Q1;
            Q1=makeQuery(id+"F10.opPattern","COPY",EDGE,{"derivedFrom":makeQuery(id+"F8.opExtrude","SWEPT_EDGE",EDGE,{"disambiguationData":[OSD([sQuery(id+"F7.wireOp",EDGE,"E32"),sQuery(id+"F7.wireOp",EDGE,"E41.4.0")])]}),"instanceName":"1"});
            var Q2;
            Q2=makeQuery(id+"F10.opPattern","COPY",EDGE,{"derivedFrom":makeQuery(id+"F8.opExtrude","SWEPT_EDGE",EDGE,{"disambiguationData":[OSD([sQuery(id+"F7.wireOp",EDGE,"E32"),sQuery(id+"F7.wireOp",EDGE,"E41.4.3")])]}),"instanceName":"1"});
            var Q3;
            Q3=makeQuery(id+"F10.opPattern","COPY",EDGE,{"derivedFrom":makeQuery(id+"F8.opExtrude","SWEPT_EDGE",EDGE,{"disambiguationData":[OSD([sQuery(id+"F7.wireOp",EDGE,"E32"),sQuery(id+"F7.wireOp",EDGE,"E41.5.0")])]}),"instanceName":"1"});
            var Q4;
            Q4=makeQuery(id+"F10.opPattern","COPY",EDGE,{"derivedFrom":makeQuery(id+"F8.opExtrude","SWEPT_EDGE",EDGE,{"disambiguationData":[OSD([sQuery(id+"F7.wireOp",EDGE,"E32"),sQuery(id+"F7.wireOp",EDGE,"E41.5.3")])]}),"instanceName":"1"});
            var Q5;
            Q5=makeQuery(id+"F10.opPattern","COPY",EDGE,{"derivedFrom":makeQuery(id+"F8.opExtrude","SWEPT_EDGE",EDGE,{"disambiguationData":[OSD([sQuery(id+"F7.wireOp",EDGE,"E32"),sQuery(id+"F7.wireOp",EDGE,"E39")])]}),"instanceName":"1"});
            var Q6;
            Q6=makeQuery(id+"F10.opPattern","COPY",EDGE,{"derivedFrom":makeQuery(id+"F8.opExtrude","SWEPT_EDGE",EDGE,{"disambiguationData":[OSD([sQuery(id+"F7.wireOp",EDGE,"E32"),sQuery(id+"F7.wireOp",EDGE,"E40")])]}),"instanceName":"1"});
            var Q7;
            Q7=makeQuery(id+"F10.opPattern","COPY",EDGE,{"derivedFrom":makeQuery(id+"F8.opExtrude","SWEPT_EDGE",EDGE,{"disambiguationData":[OSD([sQuery(id+"F7.wireOp",EDGE,"E32"),sQuery(id+"F7.wireOp",EDGE,"E41.1.0")])]}),"instanceName":"1"});
            var Q8;
            Q8=makeQuery(id+"F10.opPattern","COPY",EDGE,{"derivedFrom":makeQuery(id+"F8.opExtrude","SWEPT_EDGE",EDGE,{"disambiguationData":[OSD([sQuery(id+"F7.wireOp",EDGE,"E32"),sQuery(id+"F7.wireOp",EDGE,"E41.1.3")])]}),"instanceName":"1"});
            var Q9;
            Q9=makeQuery(id+"F10.opPattern","COPY",EDGE,{"derivedFrom":makeQuery(id+"F8.opExtrude","SWEPT_EDGE",EDGE,{"disambiguationData":[OSD([sQuery(id+"F7.wireOp",EDGE,"E32"),sQuery(id+"F7.wireOp",EDGE,"E41.2.0")])]}),"instanceName":"1"});
            var Q10;
            Q10=makeQuery(id+"F10.opPattern","COPY",EDGE,{"derivedFrom":makeQuery(id+"F8.opExtrude","SWEPT_EDGE",EDGE,{"disambiguationData":[OSD([sQuery(id+"F7.wireOp",EDGE,"E32"),sQuery(id+"F7.wireOp",EDGE,"E41.2.3")])]}),"instanceName":"1"});
            var Q11;
            Q11=makeQuery(id+"F10.opPattern","COPY",EDGE,{"derivedFrom":makeQuery(id+"F8.opExtrude","SWEPT_EDGE",EDGE,{"disambiguationData":[OSD([sQuery(id+"F7.wireOp",EDGE,"E32"),sQuery(id+"F7.wireOp",EDGE,"E41.3.0")])]}),"instanceName":"1"});
            fillet(context, id + "F21", {"entities" : qUnion([Q0, Q1, Q2, Q3, Q4, Q5, Q6, Q7, Q8, Q9, Q10, Q11]), "radius" : 31.75 * mm, "tangentPropagation" : true, "allowEdgeOverflow" : false});
        }
        {
            var Q0;
            Q0=makeQuery(id+"F10.opPattern","COPY",EDGE,{"derivedFrom":makeQuery(id+"F8.opExtrude","SWEPT_EDGE",EDGE,{"disambiguationData":[OSD([sQuery(id+"F7.wireOp",EDGE,"E41.3.2"),sQuery(id+"F7.wireOp",EDGE,"E41.3.3")])]}),"instanceName":"1"});
            var Q1;
            Q1=makeQuery(id+"F10.opPattern","COPY",EDGE,{"derivedFrom":makeQuery(id+"F8.opExtrude","SWEPT_EDGE",EDGE,{"disambiguationData":[OSD([sQuery(id+"F7.wireOp",EDGE,"E41.3.0"),sQuery(id+"F7.wireOp",EDGE,"E41.3.1")])]}),"instanceName":"1"});
            var Q2;
            Q2=makeQuery(id+"F10.opPattern","COPY",EDGE,{"derivedFrom":makeQuery(id+"F8.opExtrude","SWEPT_EDGE",EDGE,{"disambiguationData":[OSD([sQuery(id+"F7.wireOp",EDGE,"E41.2.2"),sQuery(id+"F7.wireOp",EDGE,"E41.2.3")])]}),"instanceName":"1"});
            var Q3;
            Q3=makeQuery(id+"F10.opPattern","COPY",EDGE,{"derivedFrom":makeQuery(id+"F8.opExtrude","SWEPT_EDGE",EDGE,{"disambiguationData":[OSD([sQuery(id+"F7.wireOp",EDGE,"E41.2.0"),sQuery(id+"F7.wireOp",EDGE,"E41.2.1")])]}),"instanceName":"1"});
            var Q4;
            Q4=makeQuery(id+"F10.opPattern","COPY",EDGE,{"derivedFrom":makeQuery(id+"F8.opExtrude","SWEPT_EDGE",EDGE,{"disambiguationData":[OSD([sQuery(id+"F7.wireOp",EDGE,"E41.1.2"),sQuery(id+"F7.wireOp",EDGE,"E41.1.3")])]}),"instanceName":"1"});
            var Q5;
            Q5=makeQuery(id+"F10.opPattern","COPY",EDGE,{"derivedFrom":makeQuery(id+"F8.opExtrude","SWEPT_EDGE",EDGE,{"disambiguationData":[OSD([sQuery(id+"F7.wireOp",EDGE,"E41.1.0"),sQuery(id+"F7.wireOp",EDGE,"E41.1.1")])]}),"instanceName":"1"});
            var Q6;
            Q6=makeQuery(id+"F10.opPattern","COPY",EDGE,{"derivedFrom":makeQuery(id+"F8.opExtrude","SWEPT_EDGE",EDGE,{"disambiguationData":[OSD([sQuery(id+"F7.wireOp",EDGE,"E36"),sQuery(id+"F7.wireOp",EDGE,"E40")])]}),"instanceName":"1"});
            var Q7;
            Q7=makeQuery(id+"F10.opPattern","COPY",EDGE,{"derivedFrom":makeQuery(id+"F8.opExtrude","SWEPT_EDGE",EDGE,{"disambiguationData":[OSD([sQuery(id+"F7.wireOp",EDGE,"E41.5.0"),sQuery(id+"F7.wireOp",EDGE,"E41.5.1")])]}),"instanceName":"1"});
            var Q8;
            Q8=makeQuery(id+"F10.opPattern","COPY",EDGE,{"derivedFrom":makeQuery(id+"F8.opExtrude","SWEPT_EDGE",EDGE,{"disambiguationData":[OSD([sQuery(id+"F7.wireOp",EDGE,"E41.4.2"),sQuery(id+"F7.wireOp",EDGE,"E41.4.3")])]}),"instanceName":"1"});
            var Q9;
            Q9=makeQuery(id+"F10.opPattern","COPY",EDGE,{"derivedFrom":makeQuery(id+"F8.opExtrude","SWEPT_EDGE",EDGE,{"disambiguationData":[OSD([sQuery(id+"F7.wireOp",EDGE,"E41.4.0"),sQuery(id+"F7.wireOp",EDGE,"E41.4.1")])]}),"instanceName":"1"});
            var Q10;
            Q10=makeQuery(id+"F10.opPattern","COPY",EDGE,{"derivedFrom":makeQuery(id+"F8.opExtrude","SWEPT_EDGE",EDGE,{"disambiguationData":[OSD([sQuery(id+"F7.wireOp",EDGE,"E35"),sQuery(id+"F7.wireOp",EDGE,"E39")])]}),"instanceName":"1"});
            var Q11;
            Q11=makeQuery(id+"F10.opPattern","COPY",EDGE,{"derivedFrom":makeQuery(id+"F8.opExtrude","SWEPT_EDGE",EDGE,{"disambiguationData":[OSD([sQuery(id+"F7.wireOp",EDGE,"E41.5.2"),sQuery(id+"F7.wireOp",EDGE,"E41.5.3")])]}),"instanceName":"1"});
            fillet(context, id + "F22", {"entities" : qUnion([Q0, Q1, Q2, Q3, Q4, Q5, Q6, Q7, Q8, Q9, Q10, Q11]), "radius" : 1.56 * mm, "tangentPropagation" : true, "allowEdgeOverflow" : false});
        }
    });
